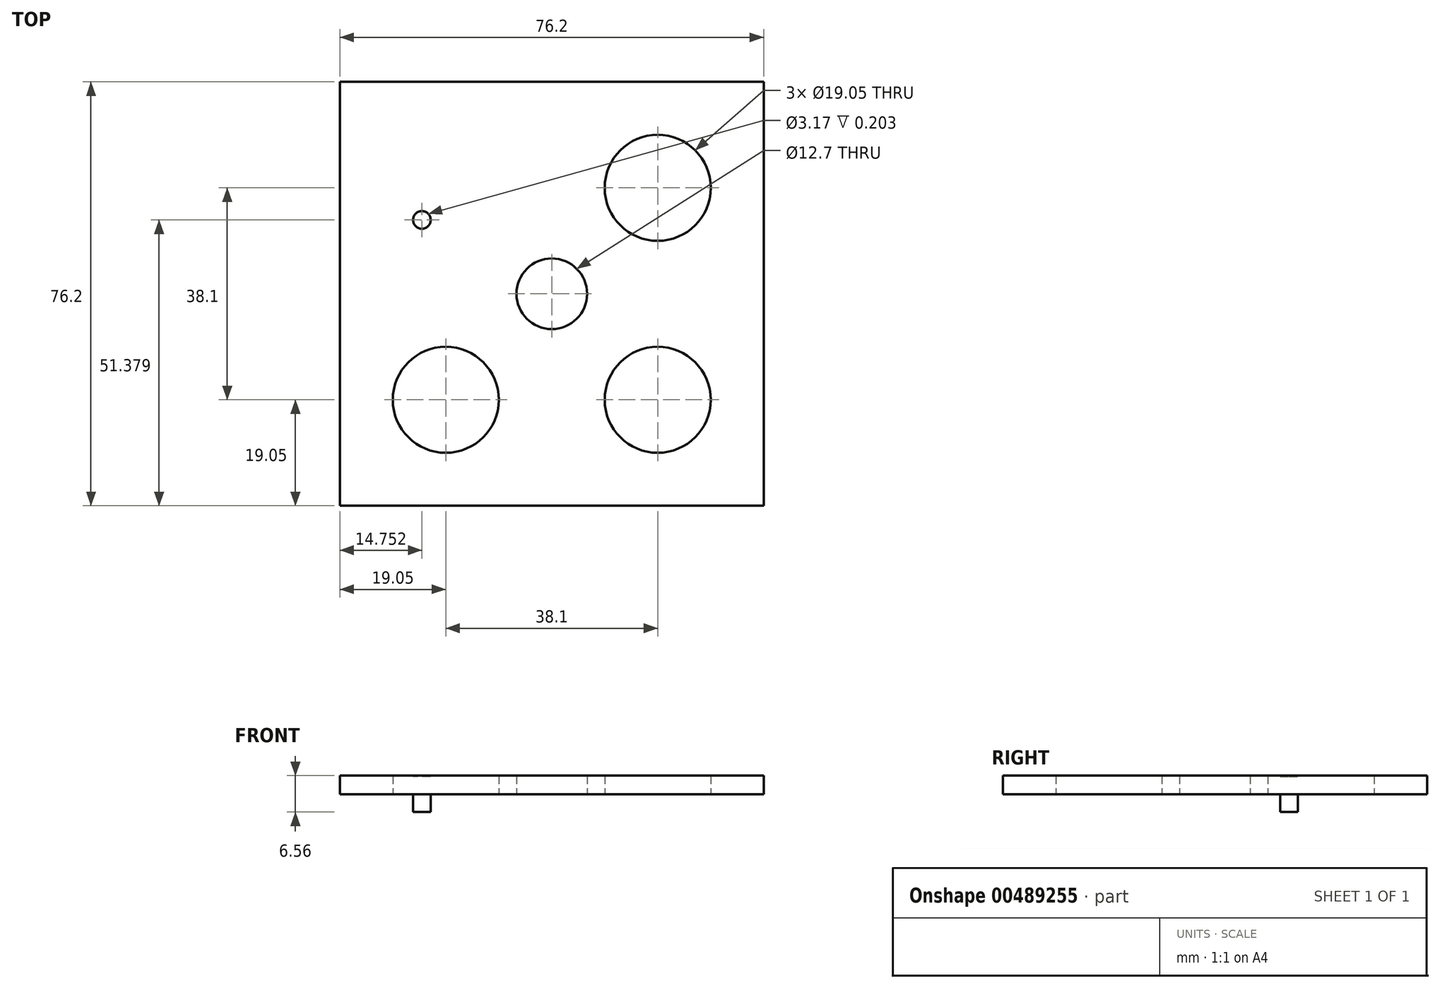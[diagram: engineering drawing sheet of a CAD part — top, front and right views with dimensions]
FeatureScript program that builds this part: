
annotation { "Feature Type Name" : "Feature", "Feature Type Description" : "" }
export const myFeature = defineFeature(function(context is Context, id is Id, definition is map)
    precondition{}
    {
        {
            var Q0;
            Q0=qCreatedBy(makeId("Top.planeOp"),FACE);
            var sketch = newSketch(context, id + "F0", { "sketchPlane" : qUnion([Q0])});
            skLineSegment(sketch, "E0.bottom", {"start": v(-38.1, 38.1) * mm, "end": v(38.1, 38.1) * mm});
            skLineSegment(sketch, "E0.top", {"start": v(-38.1, -38.1) * mm, "end": v(38.1, -38.1) * mm});
            skLineSegment(sketch, "E0.left", {"start": v(-38.1, 38.1) * mm, "end": v(-38.1, -38.1) * mm});
            skLineSegment(sketch, "E0.right", {"start": v(38.1, 38.1) * mm, "end": v(38.1, -38.1) * mm});
            skPoint(sketch, "E0.middle", {"position": v(0, 0) * mm});
            skPoint(sketch, "E1", {"position": v(19.05, 19.05) * mm});
            skLineSegment(sketch, "E2.top", {"start": v(0, -38.1) * mm, "end": v(38.1, -38.1) * mm});
            skLineSegment(sketch, "E2.right", {"start": v(38.1, 0) * mm, "end": v(38.1, -38.1) * mm});
            skPoint(sketch, "E3", {"position": v(19.05, -19.05) * mm});
            skPoint(sketch, "E4", {"position": v(-19.05, -19.05) * mm});
            skCircle(sketch, "E5", {"center": v(-23.35, 13.28) * mm, "radius": 1.59 * mm});
            skSolve(sketch);
        }
        {
            var Q0;
            Q0=makeQuery(id+"F0.imprint","IMPRINT",FACE,{"disambiguationData":[TD([[makeQuery(id+"F0.imprint","IMPRINT",EDGE,{"derivedFrom":sQuery(id+"F0.wireOp",EDGE,"E0.bottom")}),-1.0]])]});
            var Q1;
            Q1=makeQuery(id+"F0.imprint","IMPRINT",FACE,{"disambiguationData":[TD([[makeQuery(id+"F0.imprint","IMPRINT",EDGE,{"derivedFrom":sQuery(id+"F0.wireOp",EDGE,"Wfl8PiXB-tWBU-VrwB-6fQr-UqMVUnH6IEj8.bottom")}),1.0]])]});
            var Q2;
            Q2=makeQuery(id+"F0.imprint","IMPRINT",FACE,{"disambiguationData":[TD([[makeQuery(id+"F0.imprint","IMPRINT",EDGE,{"derivedFrom":sQuery(id+"F0.wireOp",EDGE,"E0.top")}),1.0]])]});
            var Q3;
            Q3=makeQuery(id+"F0.imprint","IMPRINT",FACE,{"disambiguationData":[TD([[makeQuery(id+"F0.imprint","IMPRINT",EDGE,{"derivedFrom":sQuery(id+"F0.wireOp",EDGE,"Aul39Nzb-sKAA-HBHp-FzCs-Sx4IRXZg9j8d.bottom")}),1.0]])]});
            extrude(context, id + "F1", {"entities" : qUnion([Q0, Q1, Q2, Q3]), "depth" : 3.38 * mm, "offsetDistance" : 25.4 * mm});
        }
        {
            var Q0;
            Q0=sQuery(id+"F0.wireOp",VERTEX,"E1");
            var Q1;
            Q1=sQuery(id+"F0.wireOp",VERTEX,"E3");
            var Q2;
            Q2=sQuery(id+"F0.wireOp",VERTEX,"E4");
            var Q3;
            Q3=makeQuery(id+"F1.opExtrude","SWEPT_BODY",BODY,{"disambiguationData":[OSD([sQuery(id+"F0.wireOp",EDGE,"E0.bottom"),sQuery(id+"F0.wireOp",EDGE,"E0.top"),sQuery(id+"F0.wireOp",EDGE,"E0.left"),sQuery(id+"F0.wireOp",EDGE,"E0.right")])]});
            hole(context, id + "F2", {"style" : HoleStyle.SIMPLE, "endStyle" : HoleEndStyle.THROUGH, "oppositeDirection" : true, "holeDiameter" : 19.05 * mm, "isTappedThrough" : true, "tappedDepth" : 12.7 * mm, "tapClearance" : 3, "startFromSketch" : true, "locations" : qUnion([Q0, Q1, Q2]), "scope" : qUnion([Q3])});
        }
        {
            var Q0;
            Q0=sQuery(id+"F0.wireOp",VERTEX,"E0.middle");
            var Q1;
            Q1=makeQuery(id+"F1.opExtrude","SWEPT_BODY",BODY,{"disambiguationData":[OSD([sQuery(id+"F0.wireOp",EDGE,"E0.bottom"),sQuery(id+"F0.wireOp",EDGE,"E0.top"),sQuery(id+"F0.wireOp",EDGE,"E0.left"),sQuery(id+"F0.wireOp",EDGE,"E0.right")])]});
            hole(context, id + "F3", {"style" : HoleStyle.SIMPLE, "endStyle" : HoleEndStyle.THROUGH, "oppositeDirection" : true, "holeDiameter" : 12.7 * mm, "isTappedThrough" : true, "tappedDepth" : 12.7 * mm, "tapClearance" : 3, "startFromSketch" : true, "locations" : qUnion([Q0]), "scope" : qUnion([Q1])});
        }
        {
            var Q0;
            Q0=makeQuery(id+"F0.imprint","IMPRINT",FACE,{"disambiguationData":[TD([[makeQuery(id+"F0.imprint","IMPRINT",EDGE,{"derivedFrom":sQuery(id+"F0.wireOp",EDGE,"E5")}),1.0]])]});
            extrude(context, id + "F4", {"entities" : qUnion([Q0]), "operationType" : NewBodyOperationType.ADD, "endBound" : BoundingType.SYMMETRIC, "oppositeDirection" : true, "depth" : 6.35 * mm, "offsetDistance" : 25.4 * mm});
        }
    });
